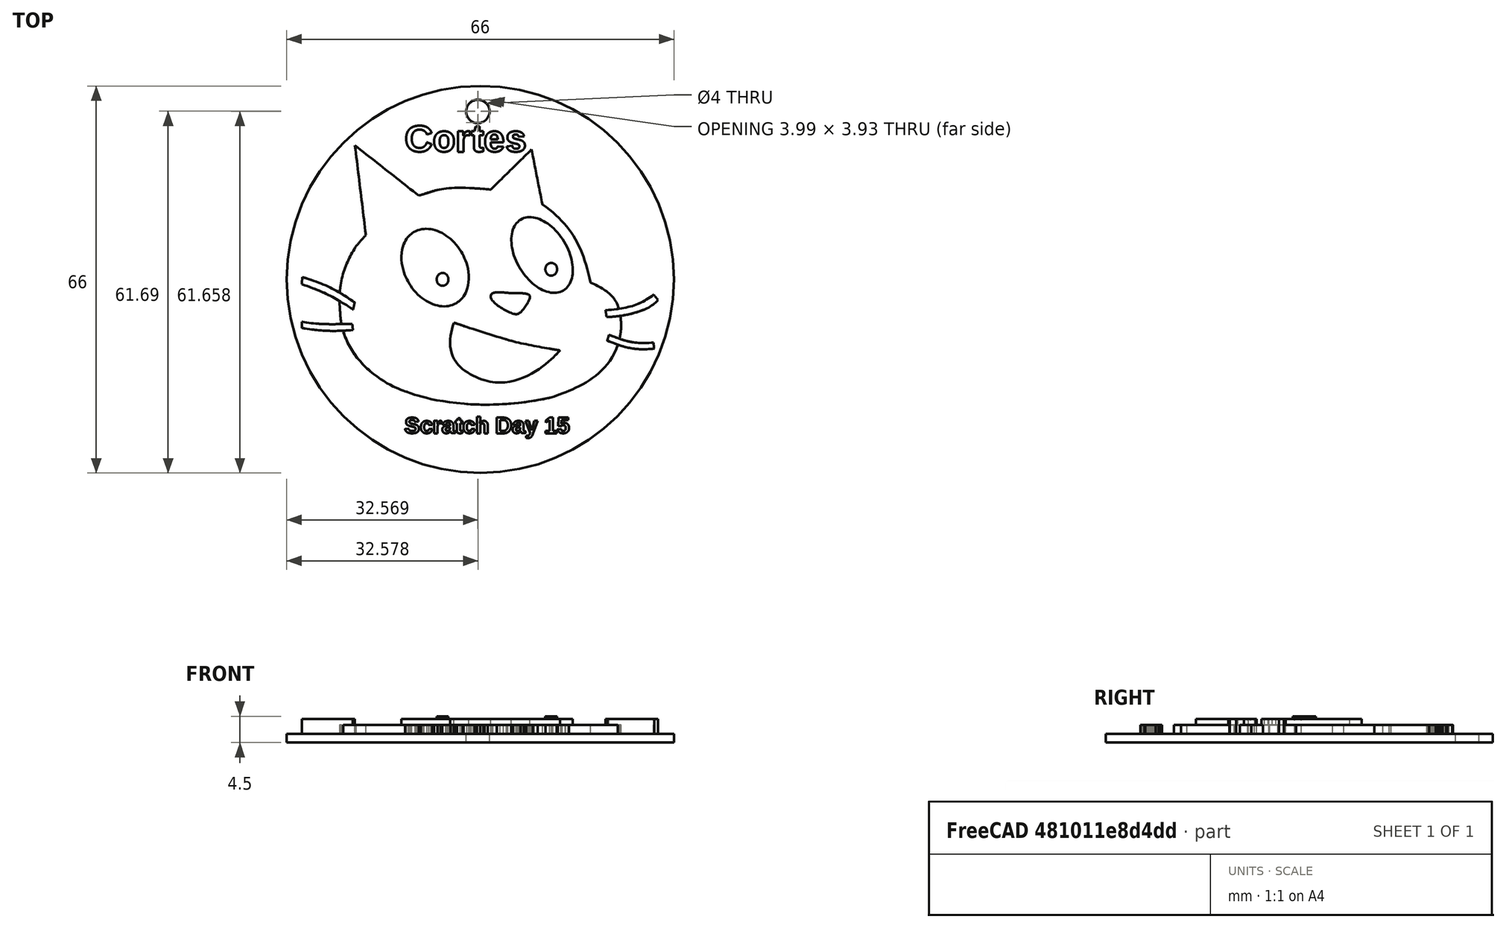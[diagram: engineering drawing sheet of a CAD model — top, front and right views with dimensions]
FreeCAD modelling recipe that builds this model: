
FCSTD DOCUMENT  (FreeCAD 0.14R3702 (Git))
Label: medalla_scratch
License: CC-BY 3.0
LicenseURL: http://creativecommons.org/licenses/by/3.0/
objects: Part::Extrusion×13, Part::Feature×11, Part::MultiFuse×2, Part::Cylinder×2, Part::Part2DObjectPython×2, App::DocumentObjectGroup×2, Part::Cut×1
note: 31 computed .brp shape members not serialized (recipe doc carries the construction recipe); baked Part::Feature solids carry a one-line shape summary decoded from their .brp

FEATURE [Part::Feature] path
  shape: bbox 48.25 x 45.35 x 2e-07 mm, 0 faces, 0 solids (baked)
FEATURE [Part::Feature] path3973_
  shape: bbox 12.16 x 13.86 x 2e-07 mm, 0 faces, 0 solids (baked)
FEATURE [Part::Feature] path3981_
  shape: bbox 11.18 x 13.57 x 2e-07 mm, 0 faces, 0 solids (baked)
FEATURE [Part::Feature] path3989_
  shape: bbox 2.026 x 2.2 x 2e-07 mm, 1 faces, 0 solids (baked)
FEATURE [Part::Feature] path3985_
  shape: bbox 2.02 x 2.197 x 2e-07 mm, 1 faces, 0 solids (baked)
FEATURE [Part::Feature] path4045_
  shape: bbox 19.5 x 11.04 x 2e-07 mm, 0 faces, 0 solids (baked)
FEATURE [Part::Feature] path3993_1_
  shape: bbox 6.742 x 3.801 x 2e-07 mm, 1 faces, 0 solids (baked)
FEATURE [Part::Feature] path001
  shape: bbox 9.018 x 5.518 x 2e-07 mm, 0 faces, 0 solids (baked)
FEATURE [Part::Feature] path002
  shape: bbox 8.682 x 1.641 x 2e-07 mm, 0 faces, 0 solids (baked)
FEATURE [Part::Feature] path003
  shape: bbox 8.914 x 3.82 x 2e-07 mm, 0 faces, 0 solids (baked)
FEATURE [Part::Feature] path004
  shape: bbox 7.988 x 2.613 x 2e-07 mm, 0 faces, 0 solids (baked)
FEATURE [Part::Extrusion] Extrude
  Base = -> path
  Dir = (0,0,2)
  Solid = true
FEATURE [Part::Extrusion] Extrude001
  Base = -> path3973_
  Dir = (0,0,3)
  Solid = true
FEATURE [Part::Extrusion] Extrude002
  Base = -> path3981_
  Dir = (0,0,3)
  Solid = true
FEATURE [Part::Extrusion] Extrude003
  Base = -> path3989_
  Dir = (0,0,3.5)
  Solid = true
FEATURE [Part::Extrusion] Extrude004
  Base = -> path3985_
  Dir = (0,0,3.5)
  Solid = true
FEATURE [Part::Extrusion] Extrude005
  Base = -> path4045_
  Dir = (0,0,3)
  Solid = true
FEATURE [Part::Extrusion] Extrude006
  Base = -> path3993_1_
  Dir = (0,0,3)
  Solid = true
FEATURE [Part::Extrusion] Extrude007
  Base = -> path001
  Dir = (0,0,3)
  Solid = true
FEATURE [Part::Extrusion] Extrude008
  Base = -> path002
  Dir = (0,0,3)
  Solid = true
FEATURE [Part::Extrusion] Extrude009
  Base = -> path003
  Dir = (0,0,3)
  Solid = true
FEATURE [Part::Extrusion] Extrude010
  Base = -> path004
  Dir = (0,0,3)
  Solid = true
FEATURE [Part::MultiFuse] Fusion
  Placement = pos=(0,0,1) rot=(0,0,1;0rad)
  Shapes = -> [Extrude,Extrude005,Extrude004,Extrude006,Extrude001,Extrude002,Extrude007,Extrude008,Extrude010,Extrude009,Extrude003]
FEATURE [Part::Cylinder] Cylinder  label="Cilindro"
  Angle = 360
  Height = 1.5
  Placement = pos=(-0.534469,1.89408,0.00142174) rot=(0,0,1;0rad)
  Radius = 33
FEATURE [Part::Part2DObjectPython] ShapeString  # Draft 2D object (typed FeaturePython)
  FontFile = <path>
  Placement = pos=(-13.454,-24.3602,0) rot=(0,0,1;0rad)
  Size = 3
  String = Scratch Day 15
  Tracking = 0
FEATURE [Part::Extrusion] Extrude011
  Base = -> ShapeString
  Dir = (0,0,2)
  Placement = pos=(0,0,1) rot=(0,0,1;0rad)
  Solid = true
FEATURE [Part::Part2DObjectPython] ShapeString001  # Draft 2D object (typed FeaturePython)
  FontFile = <path>
  Placement = pos=(-13.454,-24.3602,0) rot=(0,0,1;0rad)
  Size = 5
  String = Cortes
  Tracking = 0
FEATURE [Part::Extrusion] Extrude012
  Base = -> ShapeString001
  Dir = (0,0,2)
  Placement = pos=(0,48,1) rot=(0,0,1;0rad)
  Solid = true
FEATURE [Part::Cylinder] Cylinder001  label="Cilindro001"
  Angle = 360
  Height = 10
  Placement = pos=(-0.96752,30.4928,-3.37387) rot=(-0.987267,0.127046,0.095729;0.013586rad)
  Radius = 2
FEATURE [Part::Cut] Cut
  Base = -> Cylinder
  Tool = -> Cylinder001
FEATURE [App::DocumentObjectGroup] Grupo
FEATURE [App::DocumentObjectGroup] Grupo001
FEATURE [Part::MultiFuse] Fusion001
  Shapes = -> [Fusion,Extrude011,Cut,Extrude012]
note: 2 file-system paths scrubbed to <path> (originals preserved in the JSON sidecar)
